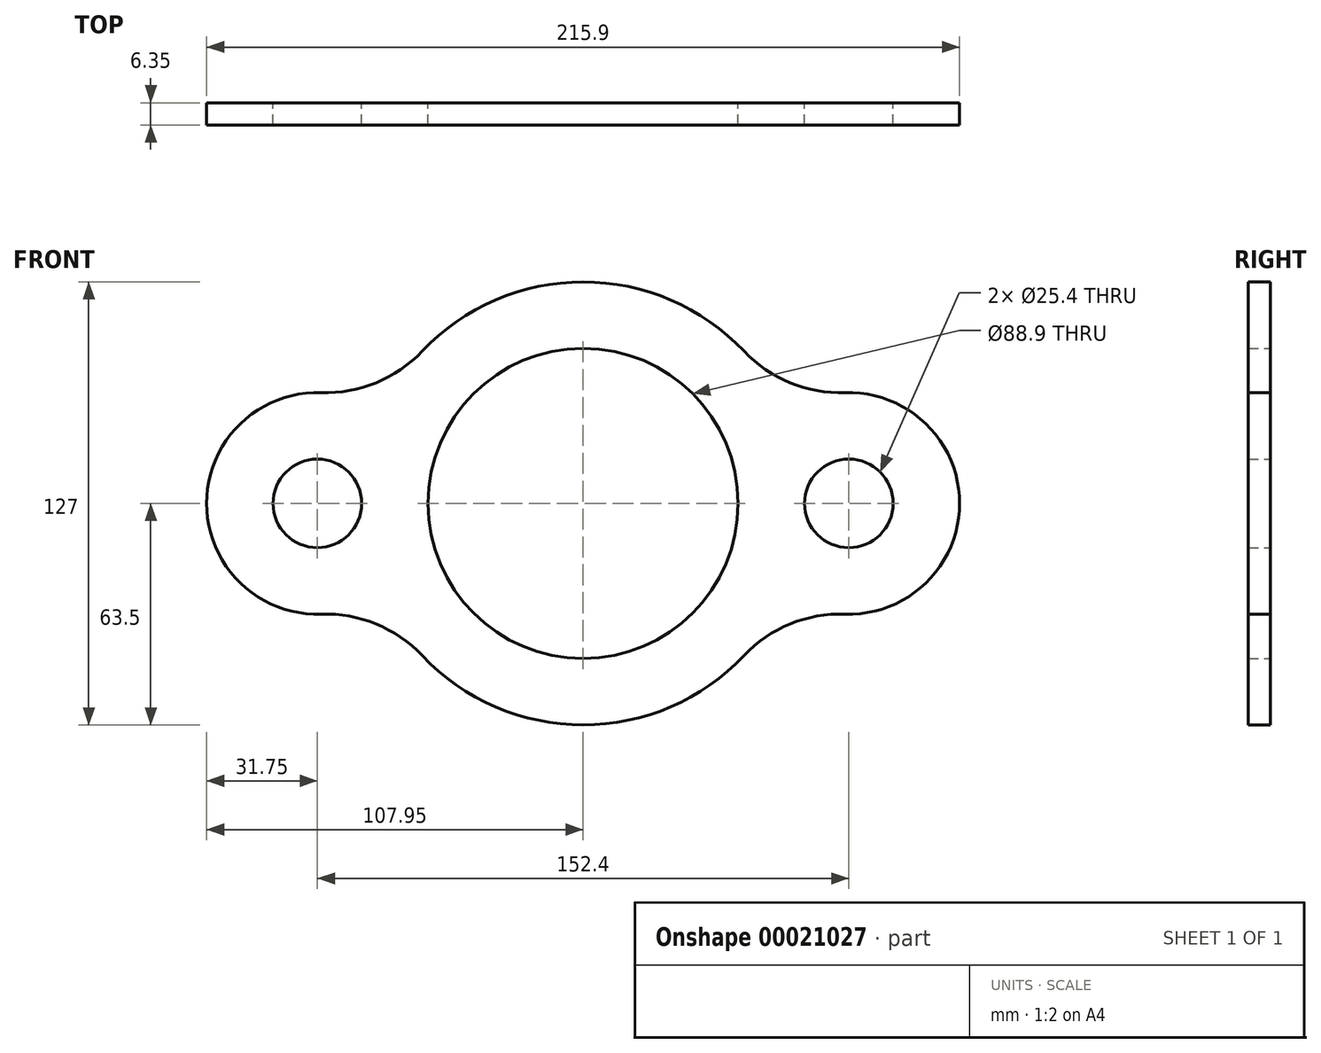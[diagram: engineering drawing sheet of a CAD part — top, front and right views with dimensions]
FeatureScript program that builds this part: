
annotation { "Feature Type Name" : "Feature", "Feature Type Description" : "" }
export const myFeature = defineFeature(function(context is Context, id is Id, definition is map)
    precondition{}
    {
        {
            var Q0;
            Q0=qCreatedBy(makeId("Front.planeOp"),FACE);
            var sketch = newSketch(context, id + "F0", { "sketchPlane" : qUnion([Q0])});
            skCircle(sketch, "E0", {"center": v(0, 0) * mm, "radius": 44.45 * mm});
            skCircle(sketch, "E1", {"center": v(-76.2, 0) * mm, "radius": 12.7 * mm});
            skCircle(sketch, "E2", {"center": v(76.2, 0) * mm, "radius": 12.7 * mm});
            skArc(sketch, "E3", {"start": v(-75.12, 31.73) * mm, "mid": v(-107.95, 0) * mm, "end": v(-75.12, -31.73) * mm});
            skArc(sketch, "E4", {"start": v(75.12, -31.73) * mm, "mid": v(107.95, 0) * mm, "end": v(75.12, 31.73) * mm});
            skArc(sketch, "E5", {"start": v(-46.14, -43.63) * mm, "mid": v(0, -63.5) * mm, "end": v(46.14, -43.63) * mm});
            skArc(sketch, "E6", {"start": v(-75.12, 31.73) * mm, "mid": v(-59.35, 34.56) * mm, "end": v(-46.14, 43.63) * mm});
            skArc(sketch, "E7", {"start": v(46.14, 43.63) * mm, "mid": v(59.35, 34.56) * mm, "end": v(75.12, 31.73) * mm});
            skArc(sketch, "E8", {"start": v(75.12, -31.73) * mm, "mid": v(59.35, -34.56) * mm, "end": v(46.14, -43.63) * mm});
            skArc(sketch, "E9", {"start": v(-46.14, -43.63) * mm, "mid": v(-59.35, -34.56) * mm, "end": v(-75.12, -31.73) * mm});
            skArc(sketch, "E10.trimOffspring", {"start": v(46.14, 43.63) * mm, "mid": v(0, 63.5) * mm, "end": v(-46.14, 43.63) * mm});
            skSolve(sketch);
        }
        {
            var Q0;
            Q0 = qSketchRegion(id + "F0", true);
            extrude(context, id + "F1", {"entities" : qUnion([Q0]), "depth" : 6.35 * mm});
        }
    });
